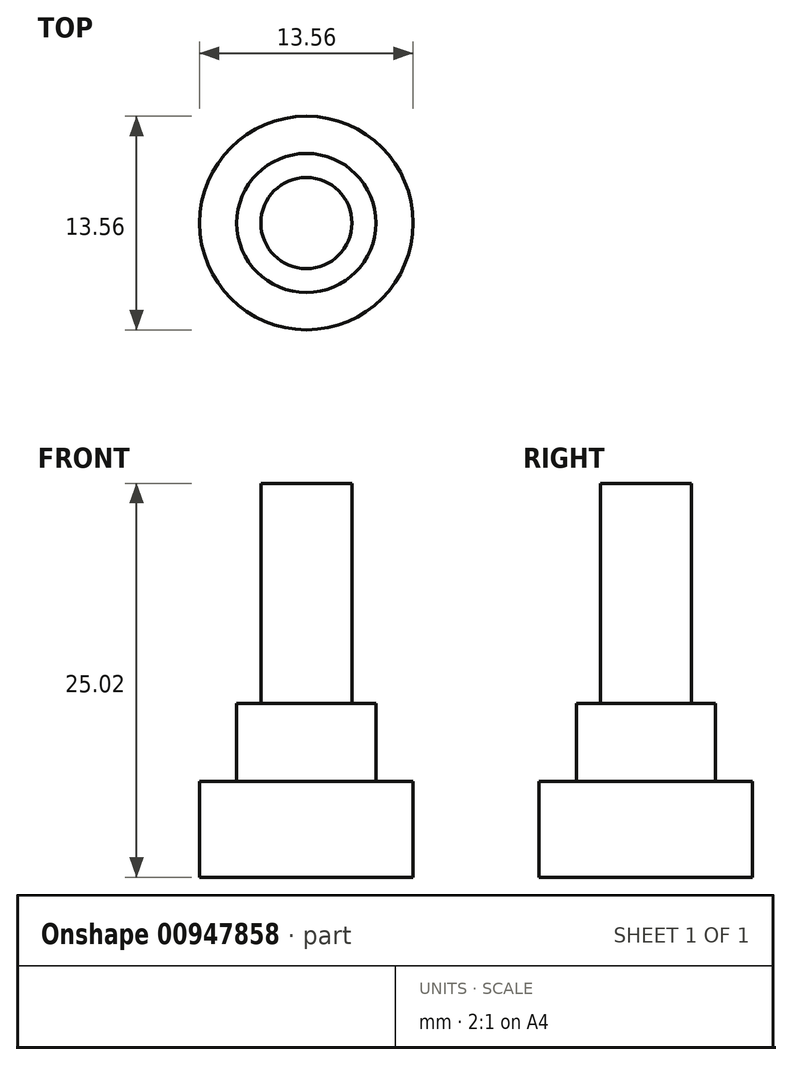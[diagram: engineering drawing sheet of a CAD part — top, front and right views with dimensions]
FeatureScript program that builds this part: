
annotation { "Feature Type Name" : "Feature", "Feature Type Description" : "" }
export const myFeature = defineFeature(function(context is Context, id is Id, definition is map)
    precondition{}
    {
        {
            var Q0;
            Q0=qCreatedBy(makeId("Front.planeOp"),FACE);
            var sketch = newSketch(context, id + "F0", { "sketchPlane" : qUnion([Q0])});
            skLineSegment(sketch, "E0", {"start": v(0, 0) * mm, "end": v(-6.78, 0) * mm});
            skLineSegment(sketch, "E1", {"start": v(-6.78, 0) * mm, "end": v(-6.78, 6.1) * mm});
            skLineSegment(sketch, "E2", {"start": v(-6.78, 6.1) * mm, "end": v(-4.42, 6.1) * mm});
            skLineSegment(sketch, "E3", {"start": v(-4.42, 6.1) * mm, "end": v(-4.42, 11.05) * mm});
            skLineSegment(sketch, "E4", {"start": v(-4.42, 11.05) * mm, "end": v(-2.9, 11.05) * mm});
            skLineSegment(sketch, "E5", {"start": v(-2.9, 11.05) * mm, "end": v(-2.9, 25.02) * mm});
            skLineSegment(sketch, "E6", {"start": v(-2.9, 25.02) * mm, "end": v(0, 25.02) * mm});
            skLineSegment(sketch, "E7", {"start": v(0, 25.02) * mm, "end": v(0, 0) * mm});
            skSolve(sketch);
        }
        {
            var Q0;
            Q0=makeQuery(id+"F0.imprint","IMPRINT",FACE,{"disambiguationData":[TD([[makeQuery(id+"F0.imprint","IMPRINT",EDGE,{"derivedFrom":sQuery(id+"F0.wireOp",EDGE,"E0")}),-1.0]])]});
            var Q1;
            Q1=sQuery(id+"F0.wireOp",EDGE,"E7");
            revolve(context, id + "F1", {"surfaceOperationType" : NewSurfaceOperationType.NEW, "entities" : qUnion([Q0]), "axis" : qUnion([Q1]), "revolveType" : RevolveType.FULL});
        }
    });
